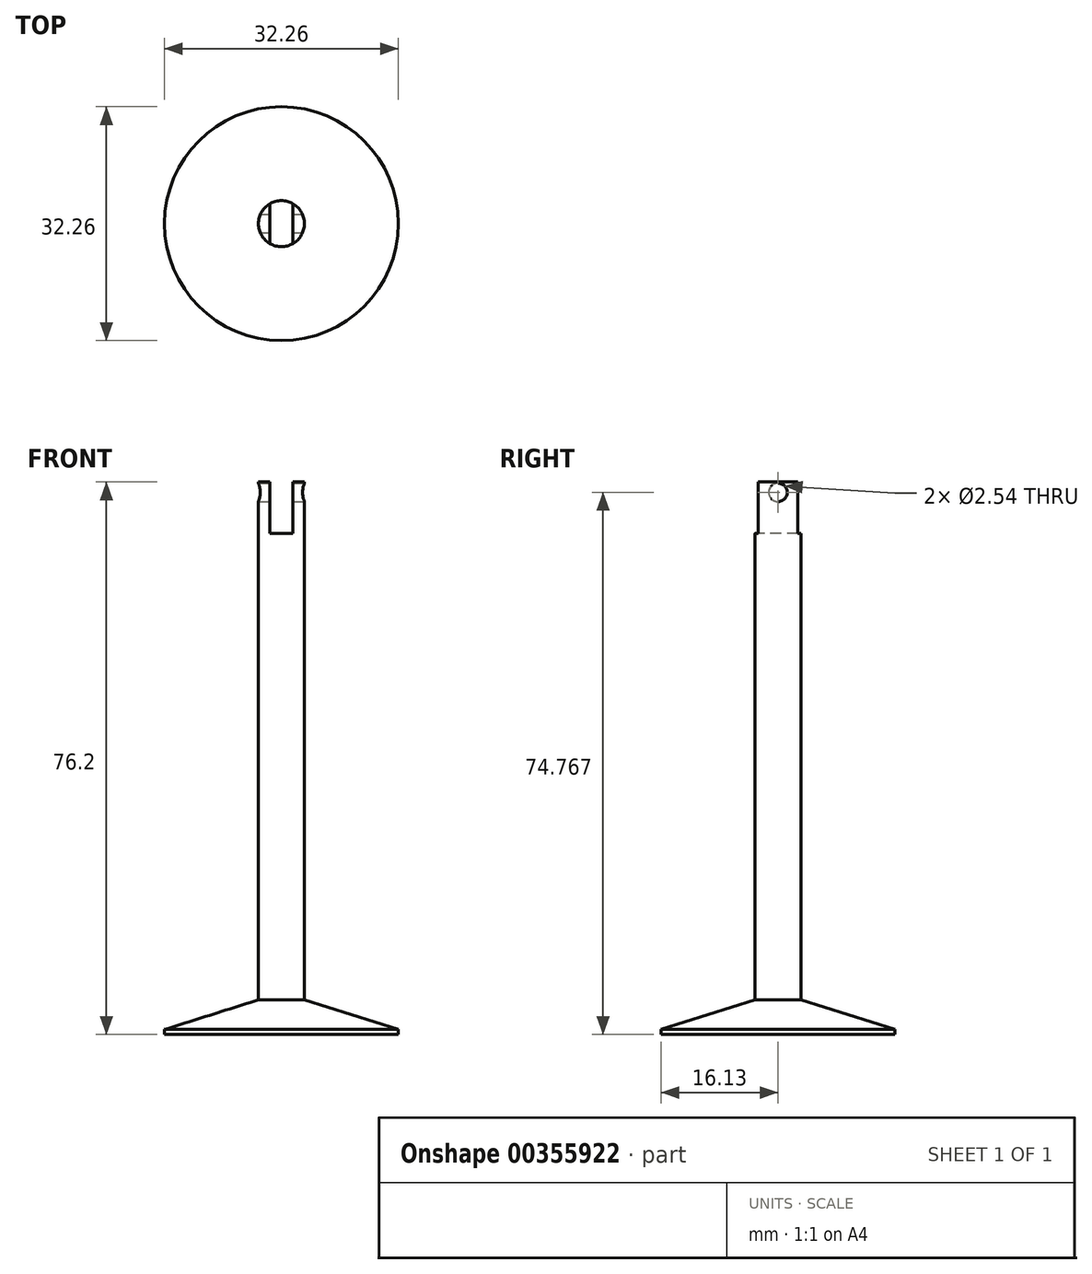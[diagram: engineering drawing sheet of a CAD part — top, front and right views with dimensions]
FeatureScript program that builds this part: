
annotation { "Feature Type Name" : "Feature", "Feature Type Description" : "" }
export const myFeature = defineFeature(function(context is Context, id is Id, definition is map)
    precondition{}
    {
        {
            var Q0;
            Q0=qCreatedBy(makeId("Top.planeOp"),FACE);
            var sketch = newSketch(context, id + "F0", { "sketchPlane" : qUnion([Q0])});
            skCircle(sketch, "E0", {"center": v(0, 0) * mm, "radius": 16.13 * mm});
            skSolve(sketch);
        }
        {
            var Q0;
            Q0=makeQuery(id+"F0.imprint","IMPRINT",FACE,{"disambiguationData":[TD([[makeQuery(id+"F0.imprint","IMPRINT",EDGE,{"derivedFrom":sQuery(id+"F0.wireOp",EDGE,"E0")}),1.0]])]});
            extrude(context, id + "F1", {"entities" : qUnion([Q0]), "depth" : 76.2 * mm});
        }
        {
            var Q0;
            Q0=qCreatedBy(makeId("Front.planeOp"),FACE);
            var sketch = newSketch(context, id + "F2", { "sketchPlane" : qUnion([Q0])});
            skLineSegment(sketch, "E1.bottom", {"start": v(3.17, 4.79) * mm, "end": v(-3.18, 4.79) * mm});
            skLineSegment(sketch, "E1.top", {"start": v(3.17, 149.2) * mm, "end": v(-3.18, 149.2) * mm});
            skLineSegment(sketch, "E1.left", {"start": v(3.17, 4.79) * mm, "end": v(3.17, 149.2) * mm});
            skLineSegment(sketch, "E1.right", {"start": v(-3.18, 4.79) * mm, "end": v(-3.18, 149.2) * mm});
            skPoint(sketch, "E1.middle", {"position": v(0, 77) * mm});
            skLineSegment(sketch, "E2", {"start": v(-3.18, 4.79) * mm, "end": v(-18.34, 0) * mm});
            skLineSegment(sketch, "E3", {"start": v(-18.34, 0) * mm, "end": v(-18.34, 89.8) * mm});
            skLineSegment(sketch, "E4", {"start": v(-18.34, 89.8) * mm, "end": v(-3.18, 89.8) * mm});
            skSolve(sketch);
        }
        {
            var Q0;
            {var subQ0=sQuery(id+"F2.wireOp",EDGE,"E2");Q0=makeQuery(id+"F2.imprint","IMPRINT",FACE,{"disambiguationData":[TD([[makeQuery(id+"F2.imprint","IMPRINT",EDGE,{"derivedFrom":subQ0}),-1.0]])]});}
            var Q1;
            Q1=makeQuery(id+"F1.opExtrude","CAP_EDGE",EDGE,{"disambiguationData":[OSD([sQuery(id+"F0.wireOp",EDGE,"E0")])],"isStart":false});
            revolve(context, id + "F3", {"operationType" : NewBodyOperationType.REMOVE, "entities" : qUnion([Q0]), "axis" : qUnion([Q1]), "revolveType" : RevolveType.FULL, "oppositeDirection" : true});
        }
        {
            var Q0;
            Q0=qCreatedBy(makeId("Front.planeOp"),FACE);
            var sketch = newSketch(context, id + "F4", { "sketchPlane" : qUnion([Q0])});
            skLineSegment(sketch, "E5.bottom", {"start": v(1.59, 71.64) * mm, "end": v(-1.59, 71.64) * mm});
            skLineSegment(sketch, "E5.top", {"start": v(1.59, 81.8) * mm, "end": v(-1.59, 81.8) * mm});
            skLineSegment(sketch, "E5.left", {"start": v(1.59, 71.64) * mm, "end": v(1.59, 81.8) * mm});
            skLineSegment(sketch, "E5.right", {"start": v(-1.59, 71.64) * mm, "end": v(-1.59, 81.8) * mm});
            skPoint(sketch, "E5.middle", {"position": v(0, 76.72) * mm});
            skSolve(sketch);
        }
        {
            var Q0;
            Q0=qSketchRegion(id+"F4",true);
            extrude(context, id + "F5", {"entities" : qUnion([Q0]), "operationType" : NewBodyOperationType.REMOVE, "endBound" : BoundingType.SYMMETRIC, "oppositeDirection" : true, "depth" : 25.4 * mm});
        }
        {
            var Q0;
            Q0=qCreatedBy(makeId("Right.planeOp"),FACE);
            var sketch = newSketch(context, id + "F6", { "sketchPlane" : qUnion([Q0])});
            skCircle(sketch, "E6", {"center": v(0, 74.77) * mm, "radius": 1.27 * mm});
            skPoint(sketch, "E7.trimOffspring.end.orphan", {"position": v(0, 73.13) * mm});
            skPoint(sketch, "E8.start.orphan", {"position": v(0, 76.4) * mm});
            skSolve(sketch);
        }
        {
            var Q0;
            Q0=makeQuery(id+"F6.imprint","IMPRINT",FACE,{"disambiguationData":[TD([[makeQuery(id+"F6.imprint","IMPRINT",EDGE,{"derivedFrom":sQuery(id+"F6.wireOp",EDGE,"E6")}),1.0]])]});
            extrude(context, id + "F7", {"entities" : qUnion([Q0]), "operationType" : NewBodyOperationType.REMOVE, "endBound" : BoundingType.SYMMETRIC, "oppositeDirection" : true, "depth" : 25.4 * mm});
        }
        {
            var Q0;
            Q0=makeQuery(id+"F5.boolean.opBoolean","COPY",FACE,{"derivedFrom":makeQuery(id+"F5.opExtrude","SWEPT_FACE",FACE,{"disambiguationData":[OSD([sQuery(id+"F4.wireOp",EDGE,"E5.bottom")])]})});
            extrude(context, id + "F8", {"entities" : qUnion([Q0]), "operationType" : NewBodyOperationType.REMOVE, "oppositeDirection" : true, "depth" : 2.54 * mm});
        }
    });
